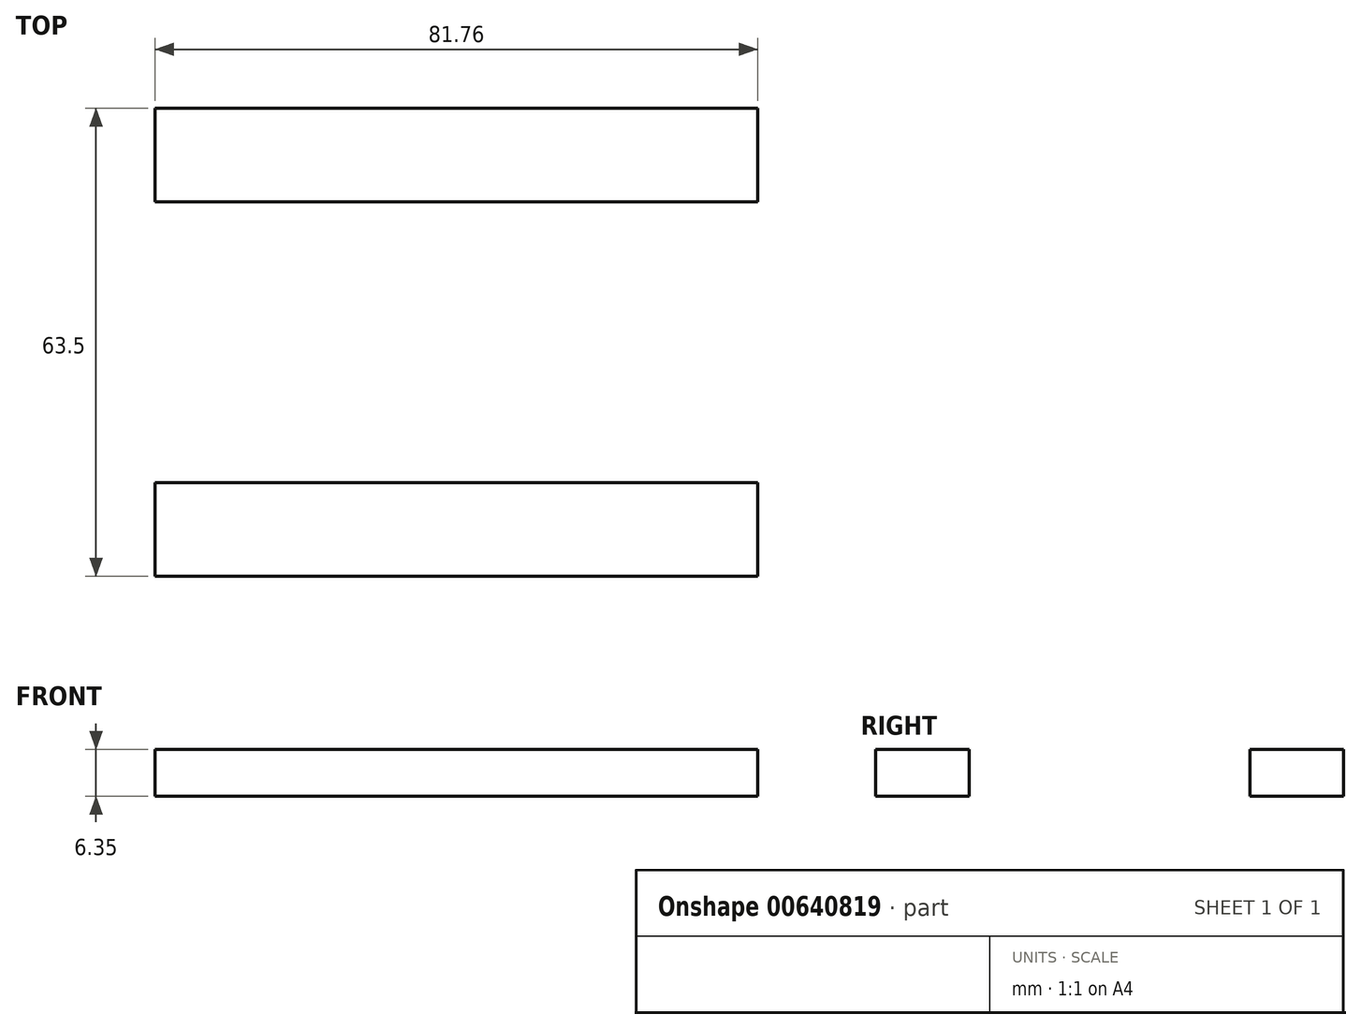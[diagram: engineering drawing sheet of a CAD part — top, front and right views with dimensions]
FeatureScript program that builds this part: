
annotation { "Feature Type Name" : "Feature", "Feature Type Description" : "" }
export const myFeature = defineFeature(function(context is Context, id is Id, definition is map)
    precondition{}
    {
        {
            var Q0;
            Q0=qCreatedBy(makeId("Top.planeOp"),FACE);
            var sketch = newSketch(context, id + "F0", { "sketchPlane" : qUnion([Q0])});
            skLineSegment(sketch, "E0", {"start": v(0, 0) * mm, "end": v(40.88, 0) * mm});
            skLineSegment(sketch, "E1", {"start": v(0, 0) * mm, "end": v(-40.88, 0) * mm});
            skSolve(sketch);
        }
        {
            var Q0;
            Q0=qCreatedBy(makeId("Right.planeOp"),FACE);
            var sketch = newSketch(context, id + "F1", { "sketchPlane" : qUnion([Q0])});
            skLineSegment(sketch, "E2.bottom", {"start": v(-31.75, 6.35) * mm, "end": v(-19.05, 6.35) * mm});
            skLineSegment(sketch, "E2.top", {"start": v(-31.75, 0) * mm, "end": v(-19.05, 0) * mm});
            skLineSegment(sketch, "E2.left", {"start": v(-31.75, 6.35) * mm, "end": v(-31.75, 0) * mm});
            skLineSegment(sketch, "E2.right", {"start": v(-19.05, 6.35) * mm, "end": v(-19.05, 0) * mm});
            skLineSegment(sketch, "E3.bottom", {"start": v(19.05, 6.35) * mm, "end": v(31.75, 6.35) * mm});
            skLineSegment(sketch, "E3.top", {"start": v(19.05, 0) * mm, "end": v(31.75, 0) * mm});
            skLineSegment(sketch, "E3.left", {"start": v(19.05, 6.35) * mm, "end": v(19.05, 0) * mm});
            skLineSegment(sketch, "E3.right", {"start": v(31.75, 6.35) * mm, "end": v(31.75, 0) * mm});
            skLineSegment(sketch, "E4", {"start": v(-19.05, 6.35) * mm, "end": v(19.05, 6.35) * mm});
            skPoint(sketch, "E5", {"position": v(0, 6.35) * mm});
            skLineSegment(sketch, "E6", {"start": v(-19.05, 0) * mm, "end": v(19.05, 0) * mm});
            skSolve(sketch);
        }
        {
            var Q0;
            Q0=makeQuery(id+"F1.imprint","IMPRINT",FACE,{"disambiguationData":[TD([[makeQuery(id+"F1.imprint","IMPRINT",EDGE,{"derivedFrom":sQuery(id+"F1.wireOp",EDGE,"E2.bottom")}),-1.0]])]});
            var Q1;
            Q1=makeQuery(id+"F1.imprint","IMPRINT",FACE,{"disambiguationData":[TD([[makeQuery(id+"F1.imprint","IMPRINT",EDGE,{"derivedFrom":sQuery(id+"F1.wireOp",EDGE,"E3.bottom")}),-1.0]])]});
            var Q2;
            Q2=sQuery(id+"F0.wireOp",VERTEX,"E0.end");
            var Q3;
            Q3=sQuery(id+"F0.wireOp",VERTEX,"E1.end");
            extrude(context, id + "F2", {"entities" : qUnion([Q0, Q1]), "endBound" : BoundingType.UP_TO_VERTEX, "depth" : 83.82 * mm, "endBoundEntityVertex" : qUnion([Q2]), "offsetDistance" : 25.4 * mm, "hasSecondDirection" : true, "secondDirectionBound" : SecondDirectionBoundingType.UP_TO_VERTEX, "secondDirectionOppositeDirection" : true, "secondDirectionDepth" : 25.4 * mm, "secondDirectionBoundEntityVertex" : qUnion([Q3])});
        }
    });
